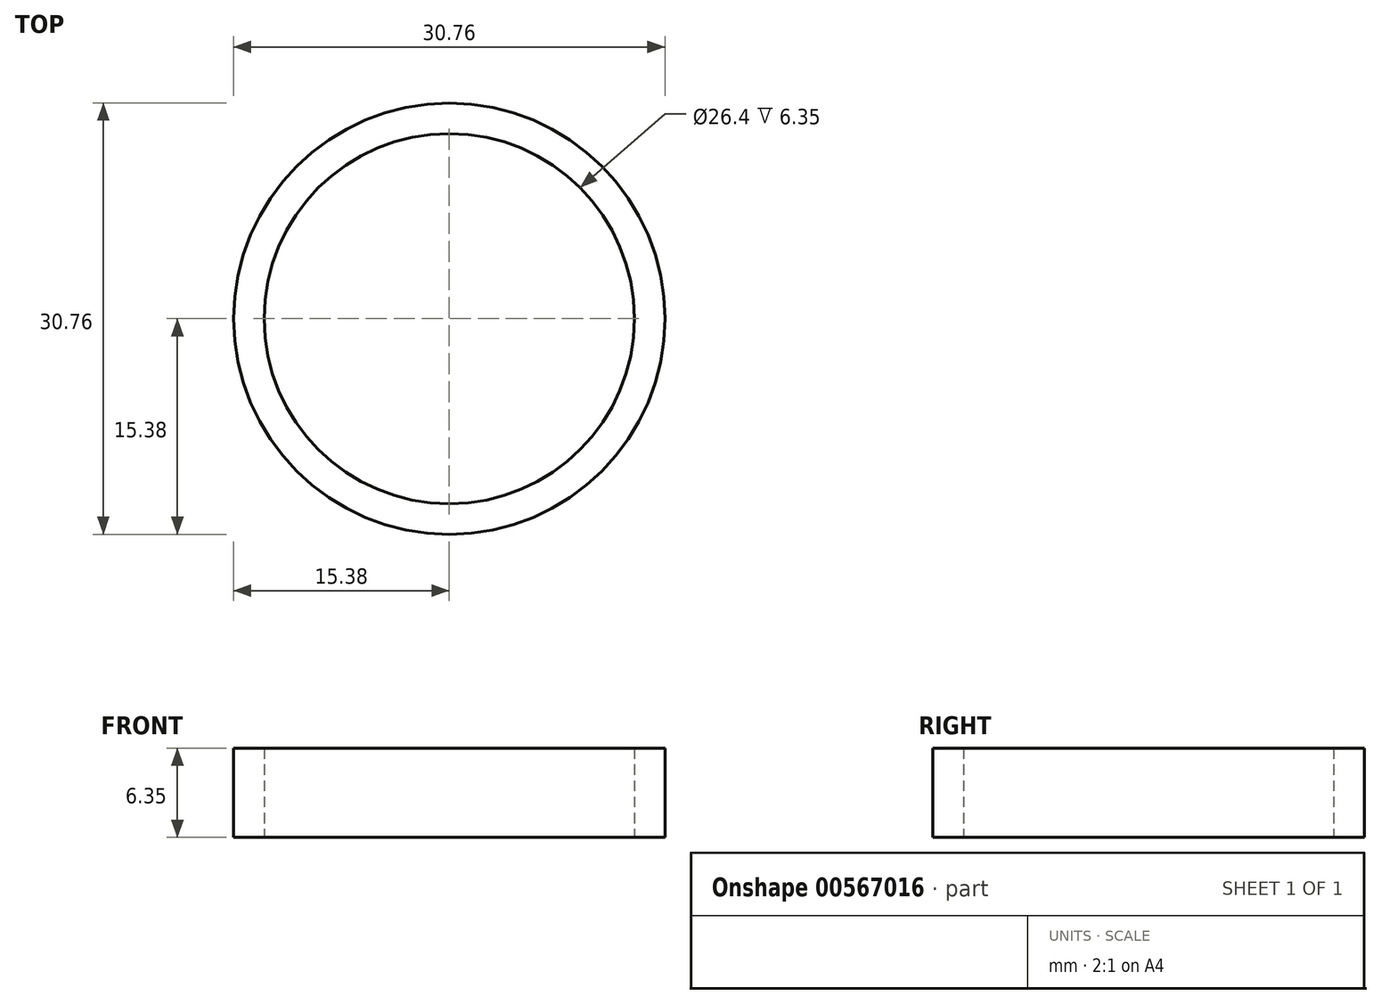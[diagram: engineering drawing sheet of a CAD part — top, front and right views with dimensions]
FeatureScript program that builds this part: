
annotation { "Feature Type Name" : "Feature", "Feature Type Description" : "" }
export const myFeature = defineFeature(function(context is Context, id is Id, definition is map)
    precondition{}
    {
        {
            var Q0;
            Q0=qCreatedBy(makeId("Top.planeOp"),FACE);
            var sketch = newSketch(context, id + "F0", { "sketchPlane" : qUnion([Q0])});
            skCircle(sketch, "E0", {"center": v(0, 0) * mm, "radius": 13.2 * mm});
            skCircle(sketch, "E1", {"center": v(0, 0) * mm, "radius": 15.38 * mm});
            skSolve(sketch);
        }
        {
            var Q0;
            Q0=makeQuery(id+"F0.imprint","IMPRINT",FACE,{"disambiguationData":[TD([[makeQuery(id+"F0.imprint","IMPRINT",EDGE,{"derivedFrom":sQuery(id+"F0.wireOp",EDGE,"E0")}),-1.0]])]});
            extrude(context, id + "F1", {"entities" : qUnion([Q0]), "depth" : 6.35 * mm, "offsetDistance" : 25.4 * mm});
        }
    });
